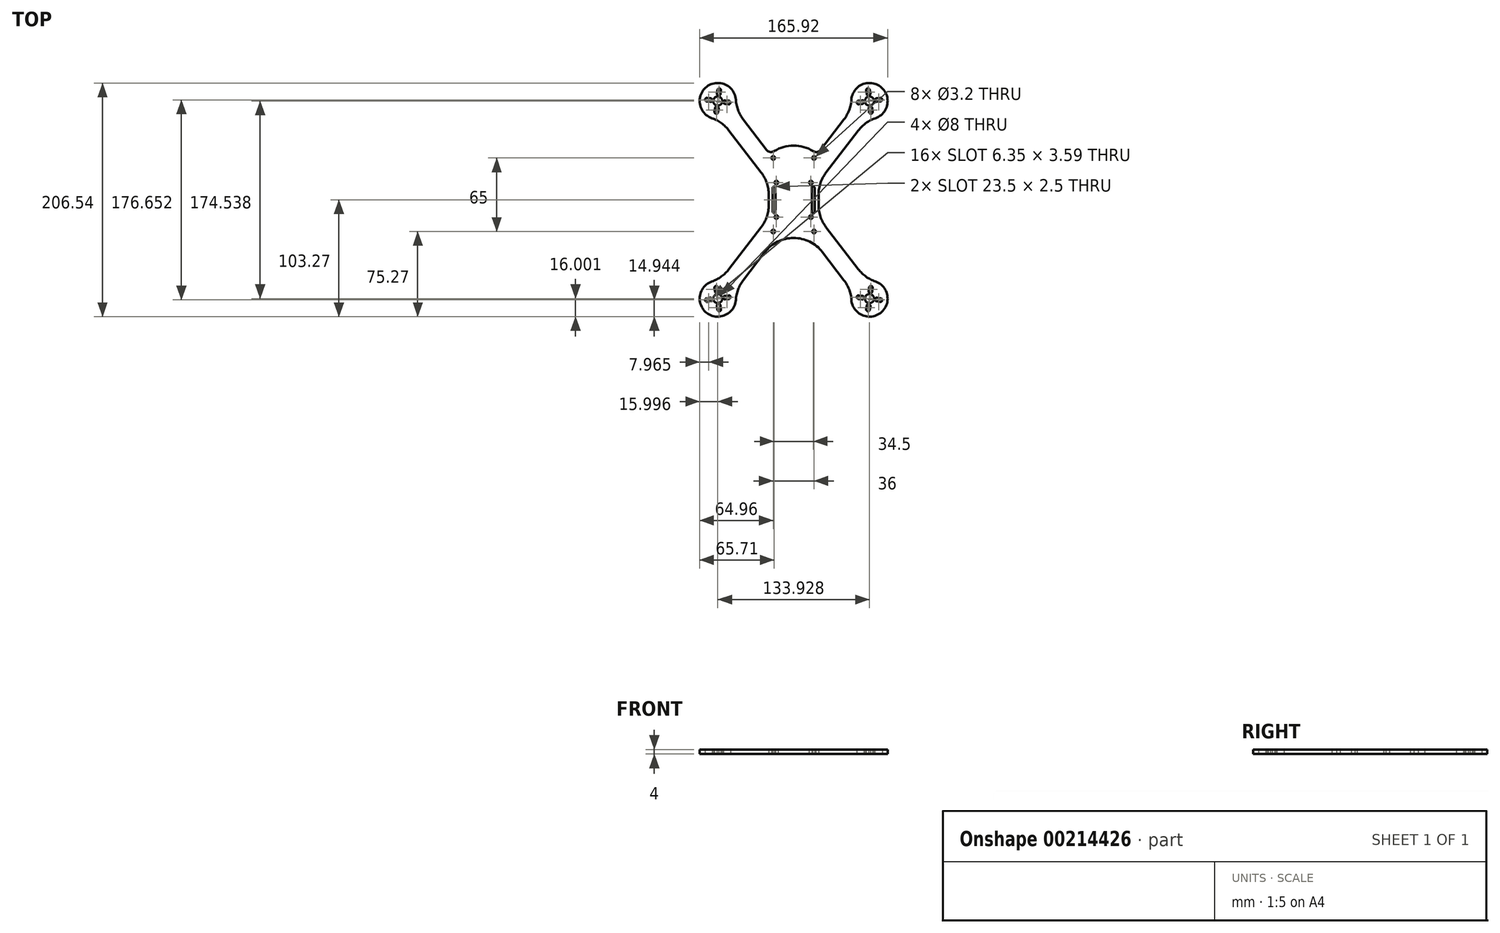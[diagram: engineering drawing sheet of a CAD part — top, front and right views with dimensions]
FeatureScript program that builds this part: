
annotation { "Feature Type Name" : "Feature", "Feature Type Description" : "" }
export const myFeature = defineFeature(function(context is Context, id is Id, definition is map)
    precondition{}
    {
        {
            var Q0;
            Q0=qCreatedBy(makeId("Top.planeOp"),FACE);
            var sketch = newSketch(context, id + "F0", { "sketchPlane" : qUnion([Q0])});
            skCircle(sketch, "E0", {"center": v(0, 0) * mm, "radius": 110 * mm, "construction": true});
            skCircle(sketch, "E1", {"center": v(-66.96, 87.27) * mm, "radius": 4 * mm});
            skArc(sketch, "E2", {"start": v(-51, 88.37) * mm, "mid": v(-76.7, 99.96) * mm, "end": v(-72.16, 72.14) * mm});
            skLineSegment(sketch, "E3.left", {"start": v(-22, 4.67) * mm, "end": v(-22, -4.67) * mm});
            skLineSegment(sketch, "E3.right", {"start": v(22, 4.67) * mm, "end": v(22, -4.67) * mm});
            skLineSegment(sketch, "E4.bottom", {"start": v(-15.25, 15.25) * mm, "end": v(15.25, 15.25) * mm, "construction": true});
            skLineSegment(sketch, "E4.top", {"start": v(-15.25, -15.25) * mm, "end": v(15.25, -15.25) * mm, "construction": true});
            skLineSegment(sketch, "E4.left", {"start": v(-15.25, 15.25) * mm, "end": v(-15.25, -15.25) * mm, "construction": true});
            skLineSegment(sketch, "E4.right", {"start": v(15.25, 15.25) * mm, "end": v(15.25, -15.25) * mm, "construction": true});
            skCircle(sketch, "E5", {"center": v(-15.25, 15.25) * mm, "radius": 1.6 * mm});
            skCircle(sketch, "E6", {"center": v(15.25, 15.25) * mm, "radius": 1.6 * mm});
            skCircle(sketch, "E7", {"center": v(15.25, -15.25) * mm, "radius": 1.6 * mm});
            skCircle(sketch, "E8", {"center": v(-15.25, -15.25) * mm, "radius": 1.6 * mm});
            skLineSegment(sketch, "E9", {"start": v(-66.96, 87.27) * mm, "end": v(0, 0) * mm, "construction": true});
            skLineSegment(sketch, "E10", {"start": v(0, 0) * mm, "end": v(66.96, 87.27) * mm, "construction": true});
            skCircle(sketch, "E11", {"center": v(66.96, 87.27) * mm, "radius": 63.5 * mm, "construction": true});
            skCircle(sketch, "E12", {"center": v(-66.96, 87.27) * mm, "radius": 63.5 * mm, "construction": true});
            skCircle(sketch, "E13.MirrorC", {"center": v(66.96, -87.27) * mm, "radius": 63.5 * mm, "construction": true});
            skCircle(sketch, "E14.MirrorC", {"center": v(-66.96, -87.27) * mm, "radius": 63.5 * mm, "construction": true});
            skLineSegment(sketch, "E15.MirrorCS", {"start": v(-66.96, -87.27) * mm, "end": v(0, 0) * mm, "construction": true});
            skLineSegment(sketch, "E16.MirrorCS", {"start": v(0, 0) * mm, "end": v(66.96, -87.27) * mm, "construction": true});
            skLineSegment(sketch, "E17", {"start": v(-57.16, -61.35) * mm, "end": v(-28.61, -24.15) * mm});
            skLineSegment(sketch, "E18", {"start": v(-57.16, 61.35) * mm, "end": v(-28.61, 24.15) * mm});
            skLineSegment(sketch, "E19", {"start": v(-44.46, 71.09) * mm, "end": v(-23.82, 44.18) * mm});
            skLineSegment(sketch, "E20.trimOffspring", {"start": v(23.82, 44.18) * mm, "end": v(44.46, 71.09) * mm});
            skLineSegment(sketch, "E21", {"start": v(28.61, -24.15) * mm, "end": v(57.16, -61.35) * mm});
            skLineSegment(sketch, "E22", {"start": v(25.39, -46.23) * mm, "end": v(44.46, -71.09) * mm});
            skLineSegment(sketch, "E23.bottom", {"start": v(-18.5, 10.5) * mm, "end": v(-16, 10.5) * mm, "construction": true});
            skLineSegment(sketch, "E23.top", {"start": v(-18.5, -10.5) * mm, "end": v(-16, -10.5) * mm, "construction": true});
            skLineSegment(sketch, "E23.left", {"start": v(-18.5, 10.5) * mm, "end": v(-18.5, -10.5) * mm});
            skLineSegment(sketch, "E23.right", {"start": v(-16, 10.5) * mm, "end": v(-16, -10.5) * mm});
            skPoint(sketch, "E24.visualSharp", {"position": v(-22, 15.53) * mm});
            skArc(sketch, "E24.filletArc", {"start": v(-22, 4.67) * mm, "mid": v(-23.7, 14.95) * mm, "end": v(-28.61, 24.15) * mm});
            skPoint(sketch, "E25.visualSharp", {"position": v(-22, -15.53) * mm});
            skArc(sketch, "E25.filletArc", {"start": v(-28.61, -24.15) * mm, "mid": v(-23.7, -14.95) * mm, "end": v(-22, -4.67) * mm});
            skArc(sketch, "E26.filletArc", {"start": v(28.61, 24.15) * mm, "mid": v(23.7, 14.95) * mm, "end": v(22, 4.67) * mm});
            skPoint(sketch, "E27.visualSharp", {"position": v(22, -15.53) * mm});
            skArc(sketch, "E27.filletArc", {"start": v(22, -4.67) * mm, "mid": v(23.7, -14.95) * mm, "end": v(28.61, -24.15) * mm});
            skLineSegment(sketch, "E28.MirrorCS", {"start": v(18.5, -10.5) * mm, "end": v(16, -10.5) * mm, "construction": true});
            skLineSegment(sketch, "E29.MirrorCS", {"start": v(18.5, 10.5) * mm, "end": v(16, 10.5) * mm, "construction": true});
            skLineSegment(sketch, "E30.MirrorCS", {"start": v(18.5, 10.5) * mm, "end": v(18.5, -10.5) * mm});
            skLineSegment(sketch, "E31.MirrorCS", {"start": v(16, 10.5) * mm, "end": v(16, -10.5) * mm});
            skArc(sketch, "E32", {"start": v(-16, 10.5) * mm, "mid": v(-17.25, 11.75) * mm, "end": v(-18.5, 10.5) * mm});
            skArc(sketch, "E33", {"start": v(-18.5, -10.5) * mm, "mid": v(-17.25, -11.75) * mm, "end": v(-16, -10.5) * mm});
            skArc(sketch, "E34", {"start": v(18.5, 10.5) * mm, "mid": v(17.25, 11.75) * mm, "end": v(16, 10.5) * mm});
            skArc(sketch, "E35", {"start": v(16, -10.5) * mm, "mid": v(17.25, -11.75) * mm, "end": v(18.5, -10.5) * mm});
            skPoint(sketch, "E36.visualSharp", {"position": v(-64.88, 71.4) * mm});
            skArc(sketch, "E36.filletArc", {"start": v(-57.16, 61.35) * mm, "mid": v(-63.86, 67.85) * mm, "end": v(-72.16, 72.14) * mm});
            skPoint(sketch, "E37.visualSharp", {"position": v(-52.18, 81.15) * mm});
            skArc(sketch, "E37.filletArc", {"start": v(-51, 88.37) * mm, "mid": v(-49, 79.25) * mm, "end": v(-44.46, 71.09) * mm});
            skPoint(sketch, "E38.start.orphan", {"position": v(-18.5, -37.25) * mm});
            skPoint(sketch, "E39.visualSharp", {"position": v(18.5, -37.25) * mm});
            skCircle(sketch, "E40", {"center": v(-18, 37) * mm, "radius": 1.6 * mm});
            skCircle(sketch, "E41.MirrorC", {"center": v(18, 37) * mm, "radius": 1.6 * mm});
            skCircle(sketch, "E42.MirrorC", {"center": v(-18, -28) * mm, "radius": 1.6 * mm});
            skCircle(sketch, "E43.MirrorC", {"center": v(18, -28) * mm, "radius": 1.6 * mm});
            skLineSegment(sketch, "E44.bottom", {"start": v(-60.31, 88) * mm, "end": v(-57.14, 87.59) * mm});
            skLineSegment(sketch, "E44.top", {"start": v(-60.73, 84.83) * mm, "end": v(-57.56, 84.42) * mm});
            skLineSegment(sketch, "E44.left", {"start": v(-60.31, 88) * mm, "end": v(-60.73, 84.83) * mm, "construction": true});
            skLineSegment(sketch, "E44.right", {"start": v(-57.14, 87.59) * mm, "end": v(-57.56, 84.42) * mm, "construction": true});
            skLineSegment(sketch, "E45", {"start": v(-66.96, 87.27) * mm, "end": v(-50.6, 85.12) * mm, "construction": true});
            skArc(sketch, "E46", {"start": v(-60.31, 88) * mm, "mid": v(-62.1, 86.63) * mm, "end": v(-60.73, 84.83) * mm});
            skArc(sketch, "E47", {"start": v(-57.56, 84.42) * mm, "mid": v(-55.76, 85.8) * mm, "end": v(-57.14, 87.59) * mm});
            skLineSegment(sketch, "E48.1.0", {"start": v(-64.53, 93.5) * mm, "end": v(-64.11, 96.68) * mm});
            skLineSegment(sketch, "E48.1.1", {"start": v(-67.28, 97.1) * mm, "end": v(-64.11, 96.68) * mm, "construction": true});
            skLineSegment(sketch, "E48.1.2", {"start": v(-67.7, 93.92) * mm, "end": v(-67.28, 97.1) * mm});
            skArc(sketch, "E48.1.3", {"start": v(-67.7, 93.92) * mm, "mid": v(-66.32, 92.13) * mm, "end": v(-64.53, 93.5) * mm});
            skArc(sketch, "E48.1.4", {"start": v(-64.11, 96.68) * mm, "mid": v(-65.49, 98.47) * mm, "end": v(-67.28, 97.1) * mm});
            skLineSegment(sketch, "E48.1.5", {"start": v(-67.7, 93.92) * mm, "end": v(-64.53, 93.5) * mm, "construction": true});
            skLineSegment(sketch, "E48.1.6", {"start": v(-66.96, 87.27) * mm, "end": v(-64.81, 103.62) * mm, "construction": true});
            skLineSegment(sketch, "E48.2.0", {"start": v(-73.2, 89.7) * mm, "end": v(-76.37, 90.12) * mm});
            skLineSegment(sketch, "E48.2.1", {"start": v(-76.79, 86.95) * mm, "end": v(-76.37, 90.12) * mm, "construction": true});
            skLineSegment(sketch, "E48.2.2", {"start": v(-73.62, 86.53) * mm, "end": v(-76.79, 86.95) * mm});
            skArc(sketch, "E48.2.3", {"start": v(-73.62, 86.53) * mm, "mid": v(-71.82, 87.9) * mm, "end": v(-73.2, 89.7) * mm});
            skArc(sketch, "E48.2.4", {"start": v(-76.37, 90.12) * mm, "mid": v(-78.17, 88.74) * mm, "end": v(-76.79, 86.95) * mm});
            skLineSegment(sketch, "E48.2.5", {"start": v(-73.62, 86.53) * mm, "end": v(-73.2, 89.7) * mm, "construction": true});
            skLineSegment(sketch, "E48.2.6", {"start": v(-66.96, 87.27) * mm, "end": v(-83.32, 89.42) * mm, "construction": true});
            skLineSegment(sketch, "E48.3.0", {"start": v(-69.4, 81.03) * mm, "end": v(-69.82, 77.86) * mm});
            skLineSegment(sketch, "E48.3.1", {"start": v(-66.64, 77.44) * mm, "end": v(-69.82, 77.86) * mm, "construction": true});
            skLineSegment(sketch, "E48.3.2", {"start": v(-66.23, 80.62) * mm, "end": v(-66.64, 77.44) * mm});
            skArc(sketch, "E48.3.3", {"start": v(-66.23, 80.62) * mm, "mid": v(-67.6, 82.41) * mm, "end": v(-69.4, 81.03) * mm});
            skArc(sketch, "E48.3.4", {"start": v(-69.82, 77.86) * mm, "mid": v(-68.44, 76.07) * mm, "end": v(-66.64, 77.44) * mm});
            skLineSegment(sketch, "E48.3.5", {"start": v(-66.23, 80.62) * mm, "end": v(-69.4, 81.03) * mm, "construction": true});
            skLineSegment(sketch, "E48.3.6", {"start": v(-66.96, 87.27) * mm, "end": v(-69.12, 70.91) * mm, "construction": true});
            skArc(sketch, "E49", {"start": v(25.39, -46.23) * mm, "mid": v(0, -33.7) * mm, "end": v(-25.39, -46.23) * mm});
            skArc(sketch, "E50", {"start": v(17.17, 43) * mm, "mid": v(0, 48) * mm, "end": v(-17.17, 43) * mm});
            skPoint(sketch, "E51.visualSharp", {"position": v(-20.83, 40.3) * mm});
            skArc(sketch, "E51.filletArc", {"start": v(-23.82, 44.18) * mm, "mid": v(-20.72, 42.3) * mm, "end": v(-17.17, 43) * mm});
            skPoint(sketch, "E52.visualSharp", {"position": v(20.83, 40.3) * mm});
            skArc(sketch, "E52.filletArc", {"start": v(17.17, 43) * mm, "mid": v(20.72, 42.3) * mm, "end": v(23.82, 44.18) * mm});
            skLineSegment(sketch, "E53.MirrorCS", {"start": v(73.62, 86.53) * mm, "end": v(76.79, 86.95) * mm});
            skLineSegment(sketch, "E54.MirrorCS", {"start": v(66.23, 80.62) * mm, "end": v(66.64, 77.44) * mm});
            skLineSegment(sketch, "E55.MirrorCS", {"start": v(60.31, 88) * mm, "end": v(57.14, 87.59) * mm});
            skArc(sketch, "E56.MirrorCS", {"start": v(64.11, 96.68) * mm, "mid": v(65.49, 98.47) * mm, "end": v(67.28, 97.1) * mm});
            skLineSegment(sketch, "E57.MirrorCS", {"start": v(67.7, 93.92) * mm, "end": v(67.28, 97.1) * mm});
            skLineSegment(sketch, "E58.MirrorCS", {"start": v(67.28, 97.1) * mm, "end": v(64.11, 96.68) * mm, "construction": true});
            skLineSegment(sketch, "E59.MirrorCS", {"start": v(64.53, 93.5) * mm, "end": v(64.11, 96.68) * mm});
            skArc(sketch, "E60.MirrorCS", {"start": v(57.56, 84.42) * mm, "mid": v(55.76, 85.8) * mm, "end": v(57.14, 87.59) * mm});
            skLineSegment(sketch, "E61.MirrorCS", {"start": v(60.31, 88) * mm, "end": v(60.73, 84.83) * mm, "construction": true});
            skLineSegment(sketch, "E62.MirrorCS", {"start": v(67.7, 93.92) * mm, "end": v(64.53, 93.5) * mm, "construction": true});
            skLineSegment(sketch, "E63.MirrorCS", {"start": v(66.23, 80.62) * mm, "end": v(69.4, 81.03) * mm, "construction": true});
            skArc(sketch, "E64.MirrorCS", {"start": v(69.82, 77.86) * mm, "mid": v(68.44, 76.07) * mm, "end": v(66.64, 77.44) * mm});
            skArc(sketch, "E65.MirrorCS", {"start": v(73.62, 86.53) * mm, "mid": v(71.82, 87.9) * mm, "end": v(73.2, 89.7) * mm});
            skLineSegment(sketch, "E66.MirrorCS", {"start": v(60.73, 84.83) * mm, "end": v(57.56, 84.42) * mm});
            skLineSegment(sketch, "E67.MirrorCS", {"start": v(73.2, 89.7) * mm, "end": v(76.37, 90.12) * mm});
            skArc(sketch, "E68.MirrorCS", {"start": v(60.31, 88) * mm, "mid": v(62.1, 86.63) * mm, "end": v(60.73, 84.83) * mm});
            skLineSegment(sketch, "E69.MirrorCS", {"start": v(69.4, 81.03) * mm, "end": v(69.82, 77.86) * mm});
            skArc(sketch, "E70.MirrorCS", {"start": v(66.23, 80.62) * mm, "mid": v(67.6, 82.41) * mm, "end": v(69.4, 81.03) * mm});
            skArc(sketch, "E71.MirrorCS", {"start": v(76.37, 90.12) * mm, "mid": v(78.17, 88.74) * mm, "end": v(76.79, 86.95) * mm});
            skLineSegment(sketch, "E72.MirrorCS", {"start": v(66.64, 77.44) * mm, "end": v(69.82, 77.86) * mm, "construction": true});
            skArc(sketch, "E73.MirrorCS", {"start": v(67.7, 93.92) * mm, "mid": v(66.32, 92.13) * mm, "end": v(64.53, 93.5) * mm});
            skLineSegment(sketch, "E74.MirrorCS", {"start": v(73.62, 86.53) * mm, "end": v(73.2, 89.7) * mm, "construction": true});
            skLineSegment(sketch, "E75.MirrorCS", {"start": v(57.14, 87.59) * mm, "end": v(57.56, 84.42) * mm, "construction": true});
            skLineSegment(sketch, "E76.MirrorCS", {"start": v(76.79, 86.95) * mm, "end": v(76.37, 90.12) * mm, "construction": true});
            skLineSegment(sketch, "E77.MirrorCS", {"start": v(66.96, 87.27) * mm, "end": v(69.12, 70.91) * mm, "construction": true});
            skCircle(sketch, "E78.MirrorC", {"center": v(66.96, 87.27) * mm, "radius": 4 * mm});
            skArc(sketch, "E79.MirrorCS", {"start": v(51, 88.37) * mm, "mid": v(76.7, 99.96) * mm, "end": v(72.16, 72.14) * mm});
            skPoint(sketch, "E80.MirrorP", {"position": v(52.18, 81.15) * mm});
            skLineSegment(sketch, "E81.MirrorCS", {"start": v(66.96, 87.27) * mm, "end": v(50.6, 85.12) * mm, "construction": true});
            skLineSegment(sketch, "E82.MirrorCS", {"start": v(66.96, 87.27) * mm, "end": v(83.32, 89.42) * mm, "construction": true});
            skLineSegment(sketch, "E83.MirrorCS", {"start": v(66.96, 87.27) * mm, "end": v(64.81, 103.62) * mm, "construction": true});
            skPoint(sketch, "E84.MirrorP", {"position": v(64.88, 71.4) * mm});
            skArc(sketch, "E85.MirrorCS", {"start": v(57.16, 61.35) * mm, "mid": v(63.86, 67.85) * mm, "end": v(72.16, 72.14) * mm});
            skArc(sketch, "E86.MirrorCS", {"start": v(51, 88.37) * mm, "mid": v(49, 79.25) * mm, "end": v(44.46, 71.09) * mm});
            skLineSegment(sketch, "E87.MirrorCS", {"start": v(-64.53, -93.5) * mm, "end": v(-64.11, -96.68) * mm});
            skArc(sketch, "E88.MirrorCS", {"start": v(-76.37, -90.12) * mm, "mid": v(-78.17, -88.74) * mm, "end": v(-76.79, -86.95) * mm});
            skLineSegment(sketch, "E89.MirrorCS", {"start": v(-67.7, -93.92) * mm, "end": v(-67.28, -97.1) * mm});
            skLineSegment(sketch, "E90.MirrorCS", {"start": v(-66.23, -80.62) * mm, "end": v(-69.4, -81.03) * mm, "construction": true});
            skLineSegment(sketch, "E91.MirrorCS", {"start": v(-60.73, -84.83) * mm, "end": v(-57.56, -84.42) * mm});
            skLineSegment(sketch, "E92.MirrorCS", {"start": v(-67.28, -97.1) * mm, "end": v(-64.11, -96.68) * mm, "construction": true});
            skLineSegment(sketch, "E93.MirrorCS", {"start": v(-76.79, -86.95) * mm, "end": v(-76.37, -90.12) * mm, "construction": true});
            skArc(sketch, "E94.MirrorCS", {"start": v(-67.7, -93.92) * mm, "mid": v(-66.32, -92.13) * mm, "end": v(-64.53, -93.5) * mm});
            skLineSegment(sketch, "E95.MirrorCS", {"start": v(-73.62, -86.53) * mm, "end": v(-76.79, -86.95) * mm});
            skLineSegment(sketch, "E96.MirrorCS", {"start": v(-60.31, -88) * mm, "end": v(-60.73, -84.83) * mm, "construction": true});
            skArc(sketch, "E97.MirrorCS", {"start": v(-60.31, -88) * mm, "mid": v(-62.1, -86.63) * mm, "end": v(-60.73, -84.83) * mm});
            skLineSegment(sketch, "E98.MirrorCS", {"start": v(-57.14, -87.59) * mm, "end": v(-57.56, -84.42) * mm, "construction": true});
            skLineSegment(sketch, "E99.MirrorCS", {"start": v(-73.2, -89.7) * mm, "end": v(-76.37, -90.12) * mm});
            skLineSegment(sketch, "E100.MirrorCS", {"start": v(-73.62, -86.53) * mm, "end": v(-73.2, -89.7) * mm, "construction": true});
            skArc(sketch, "E101.MirrorCS", {"start": v(-66.23, -80.62) * mm, "mid": v(-67.6, -82.41) * mm, "end": v(-69.4, -81.03) * mm});
            skLineSegment(sketch, "E102.MirrorCS", {"start": v(-67.7, -93.92) * mm, "end": v(-64.53, -93.5) * mm, "construction": true});
            skLineSegment(sketch, "E103.MirrorCS", {"start": v(-69.4, -81.03) * mm, "end": v(-69.82, -77.86) * mm});
            skArc(sketch, "E104.MirrorCS", {"start": v(-57.56, -84.42) * mm, "mid": v(-55.76, -85.8) * mm, "end": v(-57.14, -87.59) * mm});
            skLineSegment(sketch, "E105.MirrorCS", {"start": v(-60.31, -88) * mm, "end": v(-57.14, -87.59) * mm});
            skLineSegment(sketch, "E106.MirrorCS", {"start": v(-66.23, -80.62) * mm, "end": v(-66.64, -77.44) * mm});
            skLineSegment(sketch, "E107.MirrorCS", {"start": v(-66.64, -77.44) * mm, "end": v(-69.82, -77.86) * mm, "construction": true});
            skArc(sketch, "E108.MirrorCS", {"start": v(-64.11, -96.68) * mm, "mid": v(-65.49, -98.47) * mm, "end": v(-67.28, -97.1) * mm});
            skCircle(sketch, "E109.MirrorC", {"center": v(-66.96, -87.27) * mm, "radius": 4 * mm});
            skArc(sketch, "E110.MirrorCS", {"start": v(-69.82, -77.86) * mm, "mid": v(-68.44, -76.07) * mm, "end": v(-66.64, -77.44) * mm});
            skArc(sketch, "E111.MirrorCS", {"start": v(-73.62, -86.53) * mm, "mid": v(-71.82, -87.9) * mm, "end": v(-73.2, -89.7) * mm});
            skLineSegment(sketch, "E112.MirrorCS", {"start": v(-66.96, -87.27) * mm, "end": v(-50.6, -85.12) * mm, "construction": true});
            skLineSegment(sketch, "E113.MirrorCS", {"start": v(-66.96, -87.27) * mm, "end": v(-69.12, -70.91) * mm, "construction": true});
            skLineSegment(sketch, "E114.MirrorCS", {"start": v(-66.96, -87.27) * mm, "end": v(-64.81, -103.62) * mm, "construction": true});
            skLineSegment(sketch, "E115.MirrorCS", {"start": v(-66.96, -87.27) * mm, "end": v(-83.32, -89.42) * mm, "construction": true});
            skPoint(sketch, "E116.MirrorP", {"position": v(-52.18, -81.15) * mm});
            skArc(sketch, "E117.MirrorCS", {"start": v(-51, -88.37) * mm, "mid": v(-76.7, -99.96) * mm, "end": v(-72.16, -72.14) * mm});
            skPoint(sketch, "E118.MirrorP", {"position": v(-64.88, -71.4) * mm});
            skArc(sketch, "E119.MirrorCS", {"start": v(-57.16, -61.35) * mm, "mid": v(-63.86, -67.85) * mm, "end": v(-72.16, -72.14) * mm});
            skArc(sketch, "E120.MirrorCS", {"start": v(-51, -88.37) * mm, "mid": v(-49, -79.25) * mm, "end": v(-44.46, -71.09) * mm});
            skLineSegment(sketch, "E121", {"start": v(57.16, 61.35) * mm, "end": v(28.61, 24.15) * mm});
            skLineSegment(sketch, "E122", {"start": v(-44.46, -71.09) * mm, "end": v(-25.39, -46.23) * mm});
            skLineSegment(sketch, "E123.MirrorCS", {"start": v(60.31, -88) * mm, "end": v(57.14, -87.59) * mm});
            skLineSegment(sketch, "E124.MirrorCS", {"start": v(73.2, -89.7) * mm, "end": v(76.37, -90.12) * mm});
            skLineSegment(sketch, "E125.MirrorCS", {"start": v(60.31, -88) * mm, "end": v(60.73, -84.83) * mm, "construction": true});
            skLineSegment(sketch, "E126.MirrorCS", {"start": v(69.4, -81.03) * mm, "end": v(69.82, -77.86) * mm});
            skLineSegment(sketch, "E127.MirrorCS", {"start": v(66.23, -80.62) * mm, "end": v(66.64, -77.44) * mm});
            skArc(sketch, "E128.MirrorCS", {"start": v(60.31, -88) * mm, "mid": v(62.1, -86.63) * mm, "end": v(60.73, -84.83) * mm});
            skLineSegment(sketch, "E129.MirrorCS", {"start": v(73.62, -86.53) * mm, "end": v(73.2, -89.7) * mm, "construction": true});
            skArc(sketch, "E130.MirrorCS", {"start": v(69.82, -77.86) * mm, "mid": v(68.44, -76.07) * mm, "end": v(66.64, -77.44) * mm});
            skLineSegment(sketch, "E131.MirrorCS", {"start": v(67.7, -93.92) * mm, "end": v(67.28, -97.1) * mm});
            skArc(sketch, "E132.MirrorCS", {"start": v(76.37, -90.12) * mm, "mid": v(78.17, -88.74) * mm, "end": v(76.79, -86.95) * mm});
            skArc(sketch, "E133.MirrorCS", {"start": v(57.56, -84.42) * mm, "mid": v(55.76, -85.8) * mm, "end": v(57.14, -87.59) * mm});
            skArc(sketch, "E134.MirrorCS", {"start": v(73.62, -86.53) * mm, "mid": v(71.82, -87.9) * mm, "end": v(73.2, -89.7) * mm});
            skLineSegment(sketch, "E135.MirrorCS", {"start": v(73.62, -86.53) * mm, "end": v(76.79, -86.95) * mm});
            skLineSegment(sketch, "E136.MirrorCS", {"start": v(76.79, -86.95) * mm, "end": v(76.37, -90.12) * mm, "construction": true});
            skArc(sketch, "E137.MirrorCS", {"start": v(64.11, -96.68) * mm, "mid": v(65.49, -98.47) * mm, "end": v(67.28, -97.1) * mm});
            skLineSegment(sketch, "E138.MirrorCS", {"start": v(67.28, -97.1) * mm, "end": v(64.11, -96.68) * mm, "construction": true});
            skLineSegment(sketch, "E139.MirrorCS", {"start": v(66.64, -77.44) * mm, "end": v(69.82, -77.86) * mm, "construction": true});
            skArc(sketch, "E140.MirrorCS", {"start": v(66.23, -80.62) * mm, "mid": v(67.6, -82.41) * mm, "end": v(69.4, -81.03) * mm});
            skLineSegment(sketch, "E141.MirrorCS", {"start": v(66.23, -80.62) * mm, "end": v(69.4, -81.03) * mm, "construction": true});
            skLineSegment(sketch, "E142.MirrorCS", {"start": v(64.53, -93.5) * mm, "end": v(64.11, -96.68) * mm});
            skArc(sketch, "E143.MirrorCS", {"start": v(67.7, -93.92) * mm, "mid": v(66.32, -92.13) * mm, "end": v(64.53, -93.5) * mm});
            skLineSegment(sketch, "E144.MirrorCS", {"start": v(57.14, -87.59) * mm, "end": v(57.56, -84.42) * mm, "construction": true});
            skLineSegment(sketch, "E145.MirrorCS", {"start": v(60.73, -84.83) * mm, "end": v(57.56, -84.42) * mm});
            skLineSegment(sketch, "E146.MirrorCS", {"start": v(67.7, -93.92) * mm, "end": v(64.53, -93.5) * mm, "construction": true});
            skLineSegment(sketch, "E147.MirrorCS", {"start": v(66.96, -87.27) * mm, "end": v(50.6, -85.12) * mm, "construction": true});
            skLineSegment(sketch, "E148.MirrorCS", {"start": v(66.96, -87.27) * mm, "end": v(83.32, -89.42) * mm, "construction": true});
            skLineSegment(sketch, "E149.MirrorCS", {"start": v(66.96, -87.27) * mm, "end": v(64.81, -103.62) * mm, "construction": true});
            skCircle(sketch, "E150.MirrorC", {"center": v(66.96, -87.27) * mm, "radius": 4 * mm});
            skPoint(sketch, "E151.MirrorP", {"position": v(52.18, -81.15) * mm});
            skArc(sketch, "E152.MirrorCS", {"start": v(51, -88.37) * mm, "mid": v(76.7, -99.96) * mm, "end": v(72.16, -72.14) * mm});
            skLineSegment(sketch, "E153.MirrorCS", {"start": v(66.96, -87.27) * mm, "end": v(69.12, -70.91) * mm, "construction": true});
            skPoint(sketch, "E154.MirrorP", {"position": v(64.88, -71.4) * mm});
            skArc(sketch, "E155.MirrorCS", {"start": v(57.16, -61.35) * mm, "mid": v(63.86, -67.85) * mm, "end": v(72.16, -72.14) * mm});
            skArc(sketch, "E156.MirrorCS", {"start": v(51, -88.37) * mm, "mid": v(49, -79.25) * mm, "end": v(44.46, -71.09) * mm});
            skSolve(sketch);
        }
        {
            var Q0;
            Q0 = qSketchRegion(id + "F0", true);
            extrude(context, id + "F1", {"entities" : qUnion([Q0]), "depth" : 4 * mm});
        }
    });
